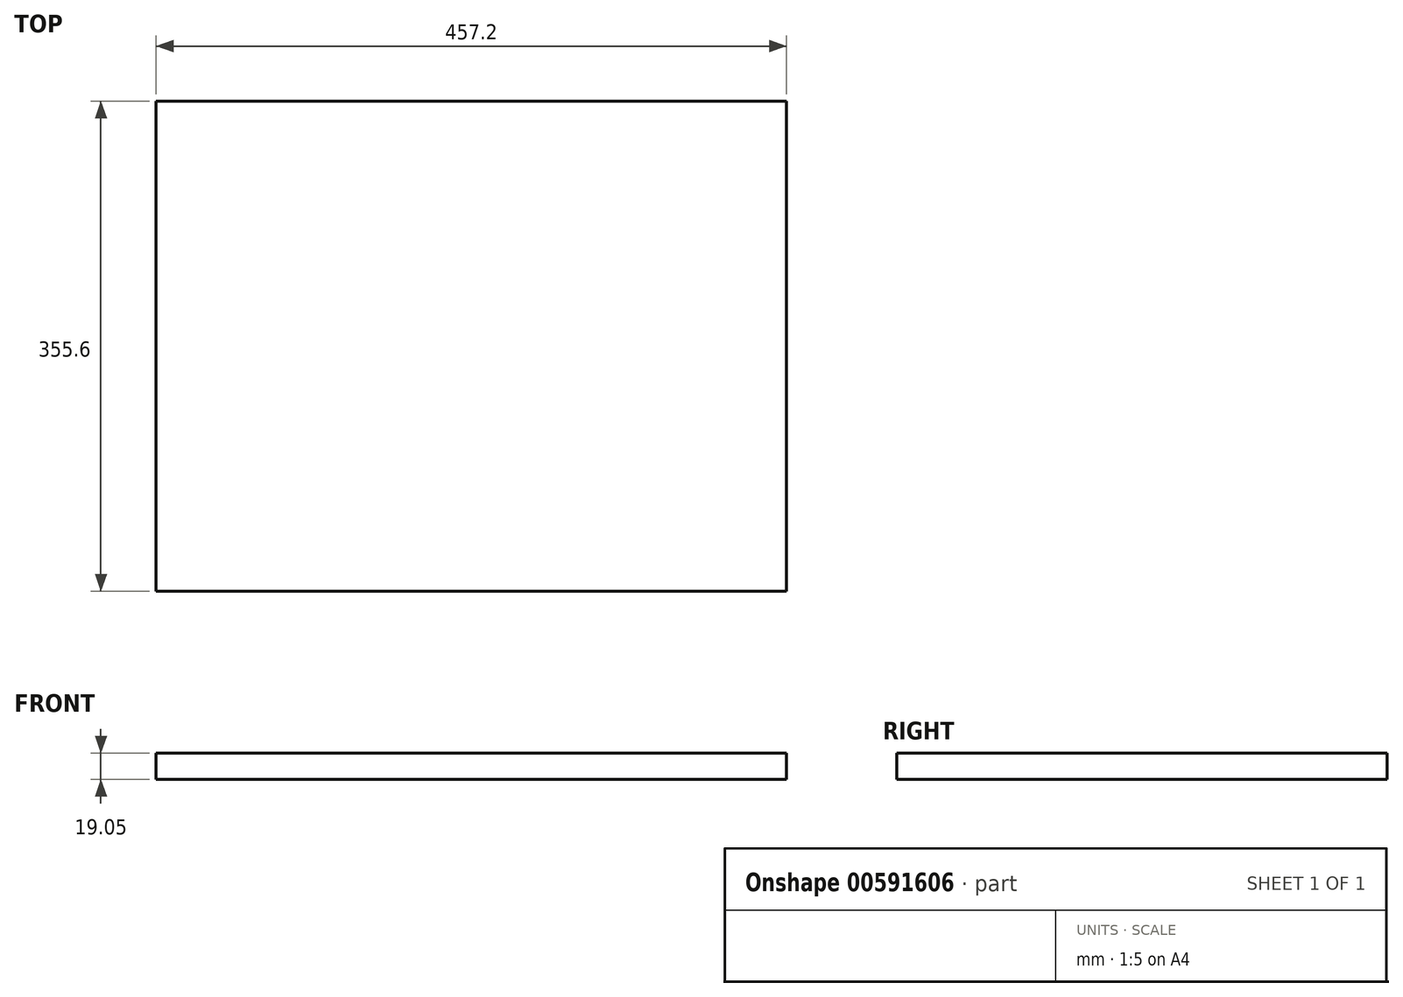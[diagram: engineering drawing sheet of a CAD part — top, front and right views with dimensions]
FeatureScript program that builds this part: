
annotation { "Feature Type Name" : "Feature", "Feature Type Description" : "" }
export const myFeature = defineFeature(function(context is Context, id is Id, definition is map)
    precondition{}
    {
        {
            var Q0;
            Q0=qCreatedBy(makeId("Top.planeOp"),FACE);
            var sketch = newSketch(context, id + "F0", { "sketchPlane" : qUnion([Q0])});
            skLineSegment(sketch, "E0.bottom", {"start": v(228.6, 168.28) * mm, "end": v(-228.6, 168.27) * mm});
            skLineSegment(sketch, "E0.top", {"start": v(228.6, -168.27) * mm, "end": v(-228.6, -168.28) * mm});
            skLineSegment(sketch, "E0.left", {"start": v(228.6, 168.28) * mm, "end": v(228.6, -168.27) * mm});
            skLineSegment(sketch, "E0.right", {"start": v(-228.6, 168.27) * mm, "end": v(-228.6, -168.28) * mm});
            skPoint(sketch, "E0.middle", {"position": v(0, 0) * mm});
            skSolve(sketch);
        }
        {
            var Q0;
            Q0=qSketchRegion(id+"F0",true);
            extrude(context, id + "F1", {"entities" : qUnion([Q0]), "depth" : 19.05 * mm, "offsetDistance" : 25.4 * mm});
        }
        {
            var Q0;
            Q0=makeQuery(id+"F1.opExtrude","SWEPT_FACE",FACE,{"disambiguationData":[OSD([sQuery(id+"F0.wireOp",EDGE,"E0.bottom")])]});
            extrude(context, id + "F2", {"entities" : qUnion([Q0]), "operationType" : NewBodyOperationType.ADD, "depth" : 19.05 * mm, "offsetDistance" : 25.4 * mm});
        }
    });
